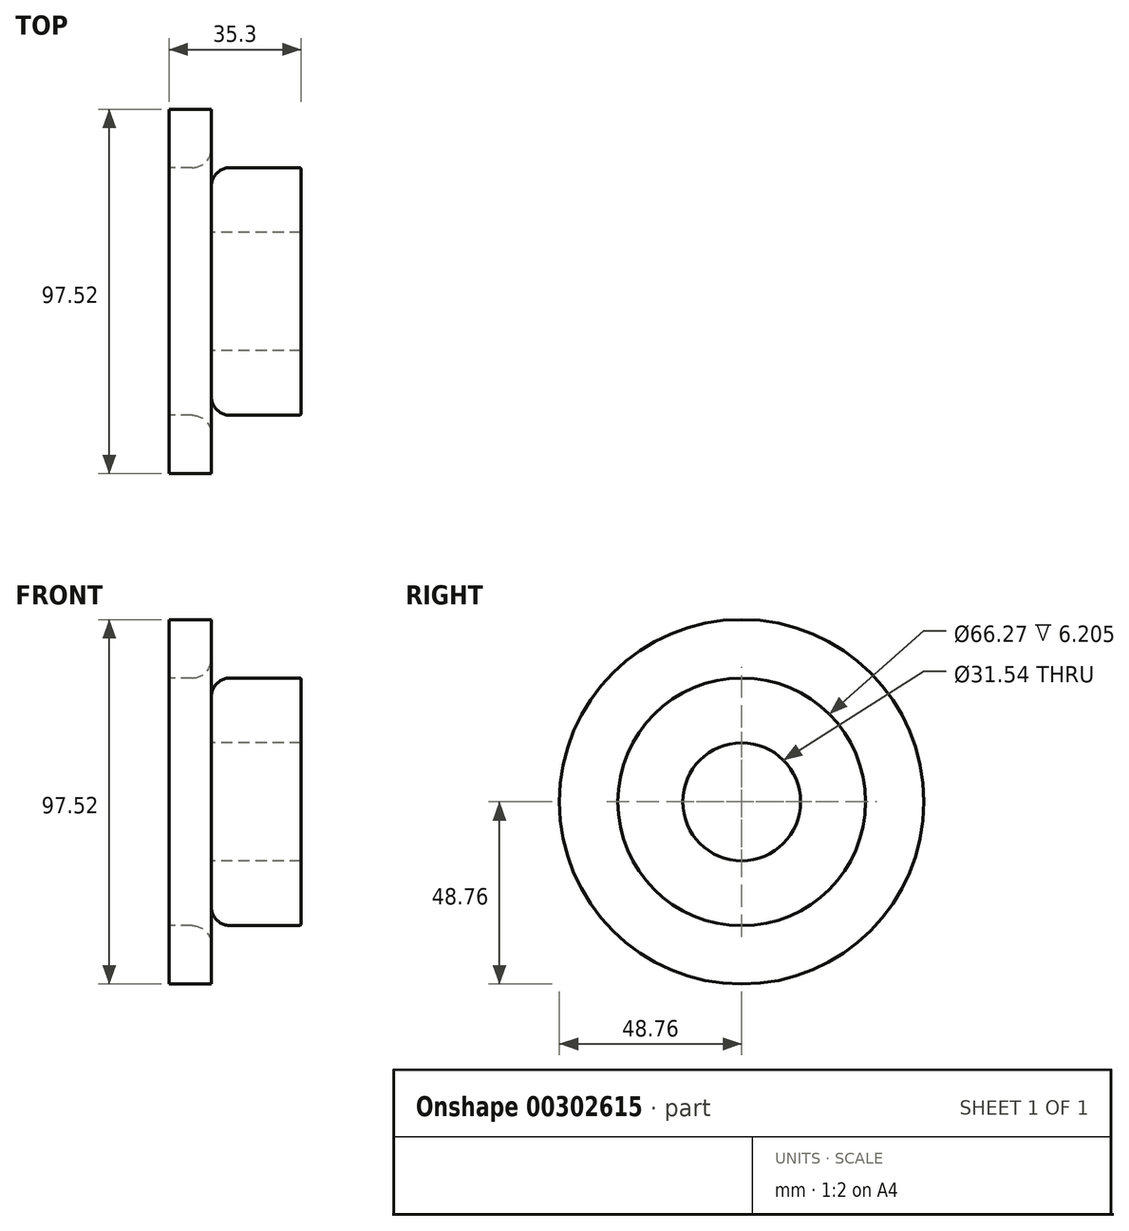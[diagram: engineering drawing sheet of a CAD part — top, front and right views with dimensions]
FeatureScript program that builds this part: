
annotation { "Feature Type Name" : "Feature", "Feature Type Description" : "" }
export const myFeature = defineFeature(function(context is Context, id is Id, definition is map)
    precondition{}
    {
        {
            var Q0;
            Q0=qCreatedBy(makeId("Front.planeOp"),FACE);
            var sketch = newSketch(context, id + "F0", { "sketchPlane" : qUnion([Q0])});
            skLineSegment(sketch, "E0", {"start": v(0, 0) * mm, "end": v(84.5, 0) * mm, "construction": true});
            skLineSegment(sketch, "E1.bottom", {"start": v(0, 15.77) * mm, "end": v(11.29, 15.77) * mm});
            skLineSegment(sketch, "E1.top", {"start": v(0, 48.76) * mm, "end": v(11.29, 48.76) * mm});
            skLineSegment(sketch, "E1.left", {"start": v(0, 15.77) * mm, "end": v(0, 48.76) * mm});
            skLineSegment(sketch, "E1.right", {"start": v(11.29, 15.77) * mm, "end": v(11.29, 48.76) * mm});
            skLineSegment(sketch, "E2.bottom", {"start": v(0, 15.77) * mm, "end": v(35.3, 15.77) * mm});
            skLineSegment(sketch, "E2.top", {"start": v(0, 33.13) * mm, "end": v(35.3, 33.13) * mm});
            skLineSegment(sketch, "E2.left", {"start": v(0, 15.77) * mm, "end": v(0, 33.13) * mm});
            skLineSegment(sketch, "E2.right", {"start": v(35.3, 15.77) * mm, "end": v(35.3, 33.13) * mm});
            skLineSegment(sketch, "E3.MirrorCS", {"start": v(0, -15.77) * mm, "end": v(11.29, -15.77) * mm});
            skLineSegment(sketch, "E4.MirrorCS", {"start": v(0, -15.77) * mm, "end": v(35.3, -15.77) * mm});
            skLineSegment(sketch, "E5.MirrorCS", {"start": v(11.29, -15.77) * mm, "end": v(11.29, -48.76) * mm});
            skLineSegment(sketch, "E6.MirrorCS", {"start": v(0, -33.13) * mm, "end": v(35.3, -33.13) * mm});
            skLineSegment(sketch, "E7.MirrorCS", {"start": v(0, -15.77) * mm, "end": v(0, -48.76) * mm});
            skLineSegment(sketch, "E8.MirrorCS", {"start": v(0, -48.76) * mm, "end": v(11.29, -48.76) * mm});
            skLineSegment(sketch, "E9.MirrorCS", {"start": v(0, -15.77) * mm, "end": v(0, -33.13) * mm});
            skLineSegment(sketch, "E10.MirrorCS", {"start": v(35.3, -15.77) * mm, "end": v(35.3, -33.13) * mm});
            skSolve(sketch);
        }
        {
            var Q0;
            {var subQ5=sQuery(id+"F0.wireOp",EDGE,"E2.right");Q0=makeQuery(id+"F0.imprint","IMPRINT",FACE,{"disambiguationData":[TD([[makeQuery(id+"F0.imprint","IMPRINT",EDGE,{"derivedFrom":subQ5}),1.0]])]});}
            var Q1;
            {var subQ0=sQuery(id+"F0.wireOp",EDGE,"E1.top");Q1=makeQuery(id+"F0.imprint","IMPRINT",FACE,{"disambiguationData":[TD([[makeQuery(id+"F0.imprint","IMPRINT",EDGE,{"derivedFrom":subQ0}),-1.0]])]});}
            var Q2;
            {var subQ5=sQuery(id+"F0.wireOp",EDGE,"E2.left");Q2=makeQuery(id+"F0.imprint","IMPRINT",FACE,{"disambiguationData":[TD([[makeQuery(id+"F0.imprint","IMPRINT",EDGE,{"derivedFrom":subQ5}),-1.0]])]});}
            var Q3;
            Q3=sQuery(id+"F0.wireOp",EDGE,"E0");
            revolve(context, id + "F1", {"entities" : qUnion([Q0, Q1, Q2]), "axis" : qUnion([Q3]), "revolveType" : RevolveType.FULL});
        }
        {
            var Q0;
            Q0=makeQuery(id+"F1.opRevolve","SWEPT_EDGE",EDGE,{"disambiguationData":[OSD([sQuery(id+"F0.wireOp",EDGE,"E1.right"),sQuery(id+"F0.wireOp",EDGE,"E2.top")])]});
            fillet(context, id + "F2", {"entities" : qUnion([Q0]), "radius" : 5.08 * mm, "tangentPropagation" : true, "allowEdgeOverflow" : false});
        }
        {
            var Q0;
            Q0=makeQuery(id+"F1.opRevolve","SWEPT_EDGE",EDGE,{"disambiguationData":[OSD([sQuery(id+"F0.wireOp",EDGE,"E2.top"),sQuery(id+"F0.wireOp",EDGE,"E2.right")])]});
            fillet(context, id + "F3", {"entities" : qUnion([Q0]), "radius" : 0.5 * mm, "tangentPropagation" : true, "allowEdgeOverflow" : false});
        }
    });
